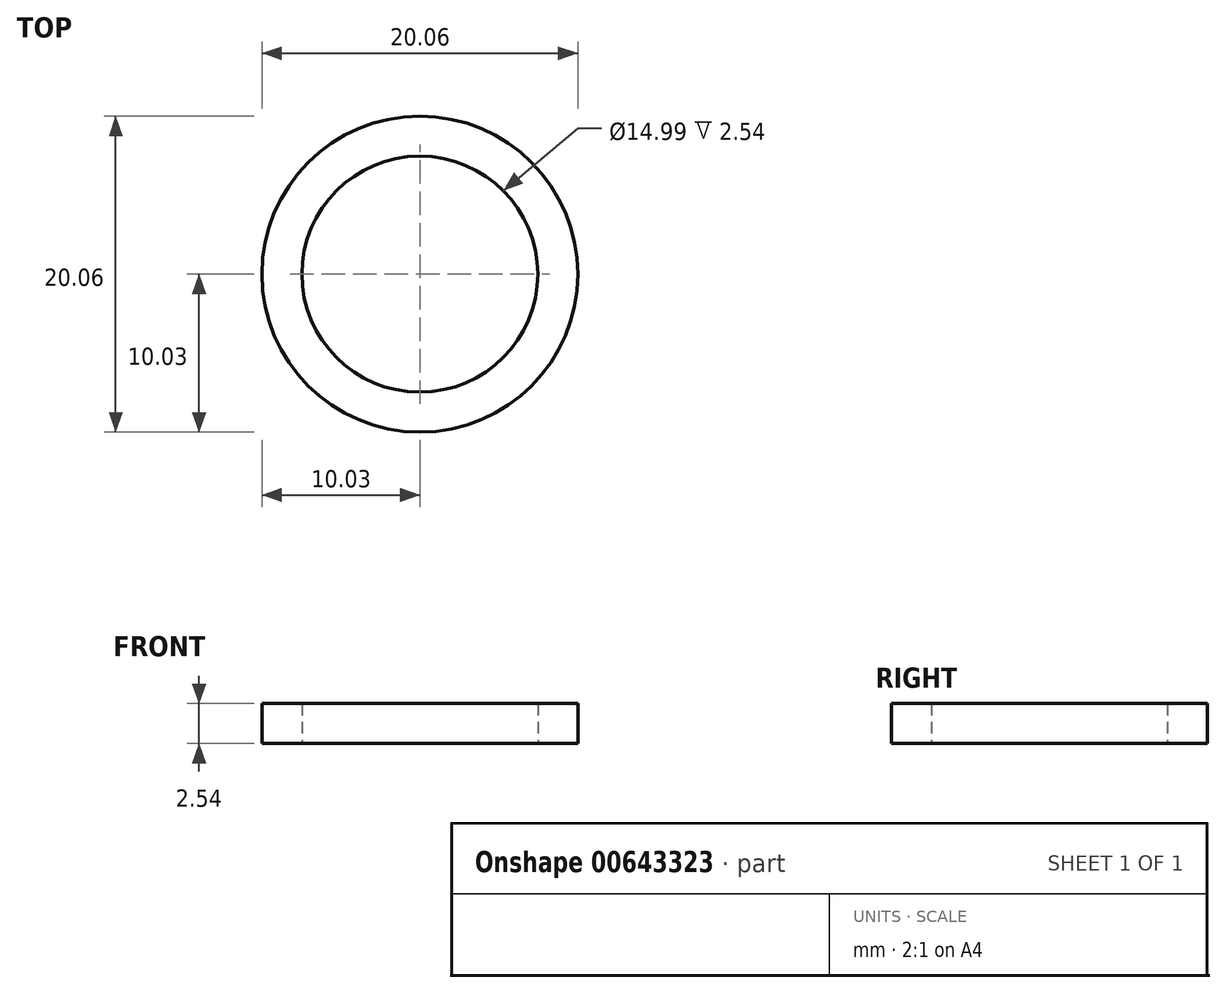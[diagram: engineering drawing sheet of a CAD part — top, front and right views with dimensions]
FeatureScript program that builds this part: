
annotation { "Feature Type Name" : "Feature", "Feature Type Description" : "" }
export const myFeature = defineFeature(function(context is Context, id is Id, definition is map)
    precondition{}
    {
        {
            var Q0;
            Q0=qCreatedBy(makeId("Top.planeOp"),FACE);
            var sketch = newSketch(context, id + "F0", { "sketchPlane" : qUnion([Q0])});
            skCircle(sketch, "E0", {"center": v(0, 0) * mm, "radius": 7.5 * mm});
            skCircle(sketch, "E1", {"center": v(0, 0) * mm, "radius": 10.03 * mm});
            skSolve(sketch);
        }
        {
            var Q0;
            Q0=makeQuery(id+"F0.imprint","IMPRINT",FACE,{"disambiguationData":[TD([[makeQuery(id+"F0.imprint","IMPRINT",EDGE,{"derivedFrom":sQuery(id+"F0.wireOp",EDGE,"E0")}),-1.0]])]});
            extrude(context, id + "F1", {"entities" : qUnion([Q0]), "depth" : 2.54 * mm, "offsetDistance" : 25.4 * mm});
        }
    });
